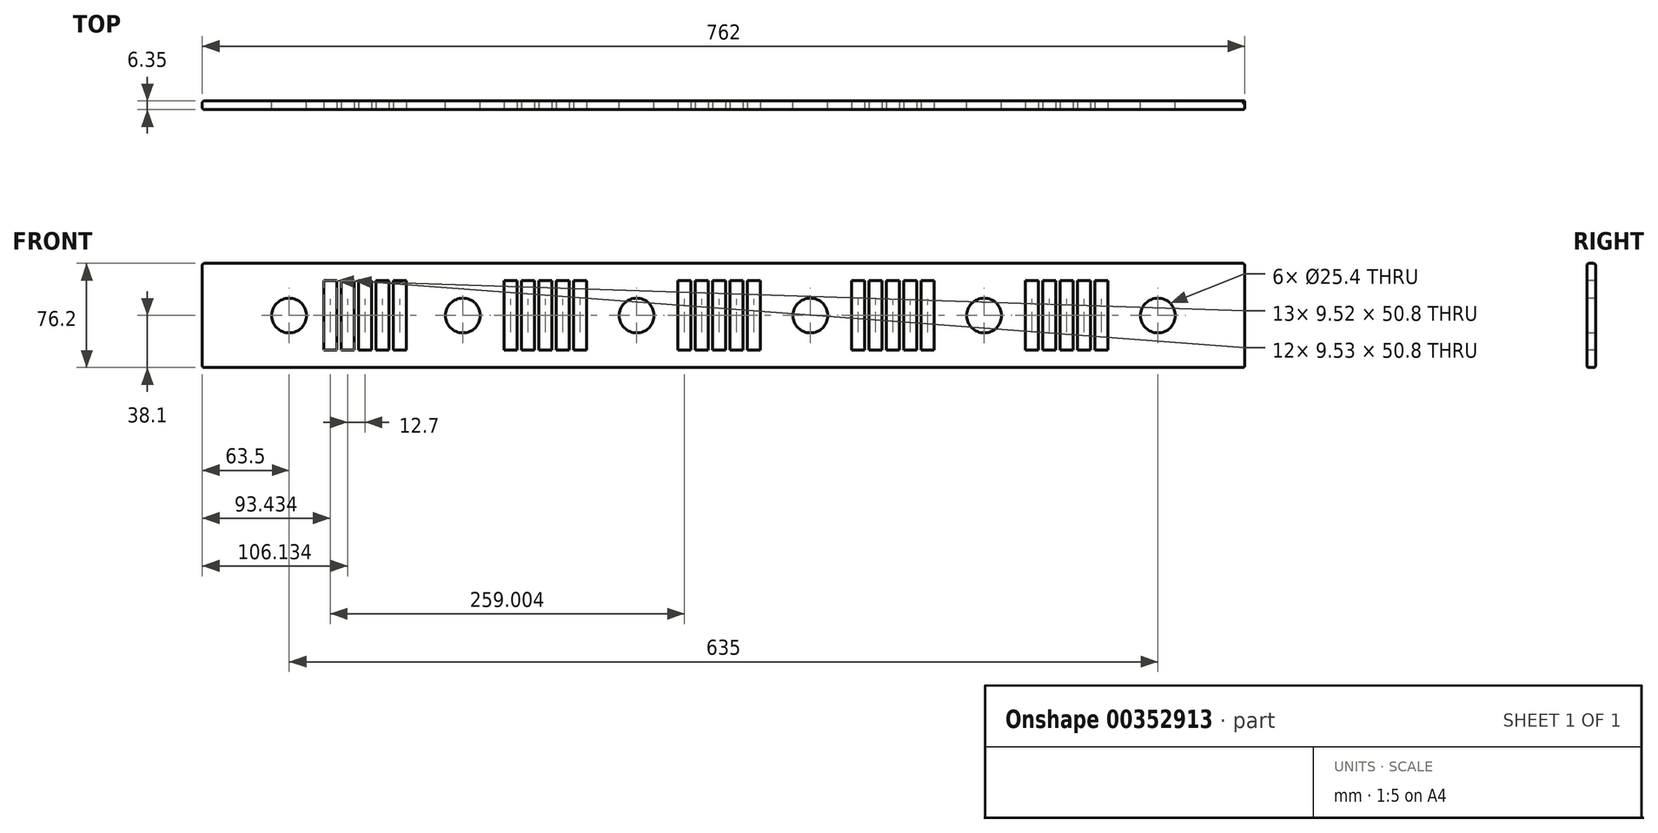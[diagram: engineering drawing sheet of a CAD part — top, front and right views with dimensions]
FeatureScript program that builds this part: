
annotation { "Feature Type Name" : "Feature", "Feature Type Description" : "" }
export const myFeature = defineFeature(function(context is Context, id is Id, definition is map)
    precondition{}
    {
        {
            var Q0;
            Q0=qCreatedBy(makeId("Front.planeOp"),FACE);
            var sketch = newSketch(context, id + "F0", { "sketchPlane" : qUnion([Q0])});
            skLineSegment(sketch, "E0.bottom", {"start": v(0, 0) * mm, "end": v(762, 0) * mm});
            skLineSegment(sketch, "E0.top", {"start": v(0, 76.2) * mm, "end": v(762, 76.2) * mm});
            skLineSegment(sketch, "E0.left", {"start": v(0, 0) * mm, "end": v(0, 76.2) * mm});
            skLineSegment(sketch, "E0.right", {"start": v(762, 0) * mm, "end": v(762, 76.2) * mm});
            skCircle(sketch, "E1", {"center": v(63.5, 38.1) * mm, "radius": 12.7 * mm});
            skPoint(sketch, "E1.centerSnap0", {"position": v(0, 38.1) * mm});
            skCircle(sketch, "E2", {"center": v(190.5, 38.1) * mm, "radius": 12.7 * mm});
            skCircle(sketch, "E3", {"center": v(317.5, 38.1) * mm, "radius": 12.7 * mm});
            skCircle(sketch, "E4", {"center": v(444.5, 38.1) * mm, "radius": 12.7 * mm});
            skCircle(sketch, "E5", {"center": v(571.5, 38.1) * mm, "radius": 12.7 * mm});
            skCircle(sketch, "E6", {"center": v(698.5, 38.1) * mm, "radius": 12.7 * mm});
            skSolve(sketch);
        }
        {
            var Q0;
            Q0=qSketchRegion(id+"F0",true);
            extrude(context, id + "F1", {"entities" : qUnion([Q0]), "depth" : 6.35 * mm});
        }
        {
            var Q0;
            Q0=makeQuery(id+"F1.opExtrude","CAP_FACE",FACE,{"disambiguationData":[OSD([sQuery(id+"F0.wireOp",EDGE,"E0.bottom"),sQuery(id+"F0.wireOp",EDGE,"E0.top"),sQuery(id+"F0.wireOp",EDGE,"E0.left"),sQuery(id+"F0.wireOp",EDGE,"E0.right"),sQuery(id+"F0.wireOp",EDGE,"E1"),sQuery(id+"F0.wireOp",EDGE,"E2"),sQuery(id+"F0.wireOp",EDGE,"E3"),sQuery(id+"F0.wireOp",EDGE,"E4"),sQuery(id+"F0.wireOp",EDGE,"E5"),sQuery(id+"F0.wireOp",EDGE,"E6")])],"isStart":false});
            var sketch = newSketch(context, id + "F2", { "sketchPlane" : qUnion([Q0])});
            skLineSegment(sketch, "E7.bottom", {"start": v(88.67, 12.7) * mm, "end": v(98.2, 12.7) * mm});
            skLineSegment(sketch, "E7.top", {"start": v(88.67, 63.5) * mm, "end": v(98.2, 63.5) * mm});
            skLineSegment(sketch, "E7.left", {"start": v(98.2, 12.7) * mm, "end": v(98.2, 63.5) * mm});
            skLineSegment(sketch, "E7.right", {"start": v(88.67, 12.7) * mm, "end": v(88.67, 63.5) * mm});
            skLineSegment(sketch, "E8.1.0.0", {"start": v(101.37, 12.7) * mm, "end": v(110.9, 12.7) * mm});
            skLineSegment(sketch, "E8.1.0.1", {"start": v(101.37, 63.5) * mm, "end": v(110.9, 63.5) * mm});
            skLineSegment(sketch, "E8.1.0.2", {"start": v(110.9, 12.7) * mm, "end": v(110.9, 63.5) * mm});
            skLineSegment(sketch, "E8.1.0.3", {"start": v(101.37, 12.7) * mm, "end": v(101.37, 63.5) * mm});
            skLineSegment(sketch, "E8.2.0.0", {"start": v(114.07, 12.7) * mm, "end": v(123.6, 12.7) * mm});
            skLineSegment(sketch, "E8.2.0.1", {"start": v(114.07, 63.5) * mm, "end": v(123.6, 63.5) * mm});
            skLineSegment(sketch, "E8.2.0.2", {"start": v(123.6, 12.7) * mm, "end": v(123.6, 63.5) * mm});
            skLineSegment(sketch, "E8.2.0.3", {"start": v(114.07, 12.7) * mm, "end": v(114.07, 63.5) * mm});
            skLineSegment(sketch, "E8.3.0.0", {"start": v(126.77, 12.7) * mm, "end": v(136.3, 12.7) * mm});
            skLineSegment(sketch, "E8.3.0.1", {"start": v(126.77, 63.5) * mm, "end": v(136.3, 63.5) * mm});
            skLineSegment(sketch, "E8.3.0.2", {"start": v(136.3, 12.7) * mm, "end": v(136.3, 63.5) * mm});
            skLineSegment(sketch, "E8.3.0.3", {"start": v(126.77, 12.7) * mm, "end": v(126.77, 63.5) * mm});
            skLineSegment(sketch, "E8.4.0.0", {"start": v(139.47, 12.7) * mm, "end": v(149, 12.7) * mm});
            skLineSegment(sketch, "E8.4.0.1", {"start": v(139.47, 63.5) * mm, "end": v(149, 63.5) * mm});
            skLineSegment(sketch, "E8.4.0.2", {"start": v(149, 12.7) * mm, "end": v(149, 63.5) * mm});
            skLineSegment(sketch, "E8.4.0.3", {"start": v(139.47, 12.7) * mm, "end": v(139.47, 63.5) * mm});
            skLineSegment(sketch, "E8.direction1", {"start": v(98.2, 12.7) * mm, "end": v(110.9, 12.7) * mm, "construction": true});
            skLineSegment(sketch, "E9.bottom", {"start": v(220.68, 12.7) * mm, "end": v(230.2, 12.7) * mm});
            skLineSegment(sketch, "E9.top", {"start": v(220.68, 63.5) * mm, "end": v(230.2, 63.5) * mm});
            skLineSegment(sketch, "E9.left", {"start": v(220.68, 12.7) * mm, "end": v(220.68, 63.5) * mm});
            skLineSegment(sketch, "E9.right", {"start": v(230.2, 12.7) * mm, "end": v(230.2, 63.5) * mm});
            skLineSegment(sketch, "E10.1.0.0", {"start": v(242.9, 12.7) * mm, "end": v(242.9, 63.5) * mm});
            skLineSegment(sketch, "E10.1.0.1", {"start": v(233.38, 12.7) * mm, "end": v(233.38, 63.5) * mm});
            skLineSegment(sketch, "E10.1.0.2", {"start": v(233.38, 63.5) * mm, "end": v(242.9, 63.5) * mm});
            skLineSegment(sketch, "E10.1.0.3", {"start": v(233.38, 12.7) * mm, "end": v(242.9, 12.7) * mm});
            skLineSegment(sketch, "E10.2.0.0", {"start": v(255.6, 12.7) * mm, "end": v(255.6, 63.5) * mm});
            skLineSegment(sketch, "E10.2.0.1", {"start": v(246.08, 12.7) * mm, "end": v(246.08, 63.5) * mm});
            skLineSegment(sketch, "E10.2.0.2", {"start": v(246.08, 63.5) * mm, "end": v(255.6, 63.5) * mm});
            skLineSegment(sketch, "E10.2.0.3", {"start": v(246.08, 12.7) * mm, "end": v(255.6, 12.7) * mm});
            skLineSegment(sketch, "E10.3.0.0", {"start": v(268.3, 12.7) * mm, "end": v(268.3, 63.5) * mm});
            skLineSegment(sketch, "E10.3.0.1", {"start": v(258.78, 12.7) * mm, "end": v(258.78, 63.5) * mm});
            skLineSegment(sketch, "E10.3.0.2", {"start": v(258.78, 63.5) * mm, "end": v(268.3, 63.5) * mm});
            skLineSegment(sketch, "E10.3.0.3", {"start": v(258.78, 12.7) * mm, "end": v(268.3, 12.7) * mm});
            skLineSegment(sketch, "E10.4.0.0", {"start": v(281, 12.7) * mm, "end": v(281, 63.5) * mm});
            skLineSegment(sketch, "E10.4.0.1", {"start": v(271.48, 12.7) * mm, "end": v(271.48, 63.5) * mm});
            skLineSegment(sketch, "E10.4.0.2", {"start": v(271.48, 63.5) * mm, "end": v(281, 63.5) * mm});
            skLineSegment(sketch, "E10.4.0.3", {"start": v(271.48, 12.7) * mm, "end": v(281, 12.7) * mm});
            skLineSegment(sketch, "E10.direction1", {"start": v(230.2, 12.7) * mm, "end": v(242.9, 12.7) * mm, "construction": true});
            skLineSegment(sketch, "E11.bottom", {"start": v(347.68, 12.7) * mm, "end": v(357.2, 12.7) * mm});
            skLineSegment(sketch, "E11.top", {"start": v(347.68, 63.5) * mm, "end": v(357.2, 63.5) * mm});
            skLineSegment(sketch, "E11.left", {"start": v(347.68, 12.7) * mm, "end": v(347.68, 63.5) * mm});
            skLineSegment(sketch, "E11.right", {"start": v(357.2, 12.7) * mm, "end": v(357.2, 63.5) * mm});
            skLineSegment(sketch, "E12.1.0.0", {"start": v(369.9, 12.7) * mm, "end": v(369.9, 63.5) * mm});
            skLineSegment(sketch, "E12.1.0.1", {"start": v(360.38, 12.7) * mm, "end": v(369.9, 12.7) * mm});
            skLineSegment(sketch, "E12.1.0.2", {"start": v(360.38, 12.7) * mm, "end": v(360.38, 63.5) * mm});
            skLineSegment(sketch, "E12.1.0.3", {"start": v(360.38, 63.5) * mm, "end": v(369.9, 63.5) * mm});
            skLineSegment(sketch, "E12.2.0.0", {"start": v(382.6, 12.7) * mm, "end": v(382.6, 63.5) * mm});
            skLineSegment(sketch, "E12.2.0.1", {"start": v(373.08, 12.7) * mm, "end": v(382.6, 12.7) * mm});
            skLineSegment(sketch, "E12.2.0.2", {"start": v(373.08, 12.7) * mm, "end": v(373.08, 63.5) * mm});
            skLineSegment(sketch, "E12.2.0.3", {"start": v(373.08, 63.5) * mm, "end": v(382.6, 63.5) * mm});
            skLineSegment(sketch, "E12.3.0.0", {"start": v(395.3, 12.7) * mm, "end": v(395.3, 63.5) * mm});
            skLineSegment(sketch, "E12.3.0.1", {"start": v(385.78, 12.7) * mm, "end": v(395.3, 12.7) * mm});
            skLineSegment(sketch, "E12.3.0.2", {"start": v(385.78, 12.7) * mm, "end": v(385.78, 63.5) * mm});
            skLineSegment(sketch, "E12.3.0.3", {"start": v(385.78, 63.5) * mm, "end": v(395.3, 63.5) * mm});
            skLineSegment(sketch, "E12.4.0.0", {"start": v(408, 12.7) * mm, "end": v(408, 63.5) * mm});
            skLineSegment(sketch, "E12.4.0.1", {"start": v(398.48, 12.7) * mm, "end": v(408, 12.7) * mm});
            skLineSegment(sketch, "E12.4.0.2", {"start": v(398.48, 12.7) * mm, "end": v(398.48, 63.5) * mm});
            skLineSegment(sketch, "E12.4.0.3", {"start": v(398.48, 63.5) * mm, "end": v(408, 63.5) * mm});
            skLineSegment(sketch, "E12.direction1", {"start": v(357.2, 12.7) * mm, "end": v(369.9, 12.7) * mm, "construction": true});
            skLineSegment(sketch, "E13.bottom", {"start": v(474.68, 12.7) * mm, "end": v(484.2, 12.7) * mm});
            skLineSegment(sketch, "E13.top", {"start": v(474.68, 63.5) * mm, "end": v(484.2, 63.5) * mm});
            skLineSegment(sketch, "E13.left", {"start": v(474.68, 12.7) * mm, "end": v(474.68, 63.5) * mm});
            skLineSegment(sketch, "E13.right", {"start": v(484.2, 12.7) * mm, "end": v(484.2, 63.5) * mm});
            skLineSegment(sketch, "E14.1.0.0", {"start": v(487.38, 12.7) * mm, "end": v(487.38, 63.5) * mm});
            skLineSegment(sketch, "E14.1.0.1", {"start": v(496.9, 12.7) * mm, "end": v(496.9, 63.5) * mm});
            skLineSegment(sketch, "E14.1.0.2", {"start": v(487.38, 12.7) * mm, "end": v(496.9, 12.7) * mm});
            skLineSegment(sketch, "E14.1.0.3", {"start": v(487.38, 63.5) * mm, "end": v(496.9, 63.5) * mm});
            skLineSegment(sketch, "E14.2.0.0", {"start": v(500.08, 12.7) * mm, "end": v(500.08, 63.5) * mm});
            skLineSegment(sketch, "E14.2.0.1", {"start": v(509.6, 12.7) * mm, "end": v(509.6, 63.5) * mm});
            skLineSegment(sketch, "E14.2.0.2", {"start": v(500.08, 12.7) * mm, "end": v(509.6, 12.7) * mm});
            skLineSegment(sketch, "E14.2.0.3", {"start": v(500.08, 63.5) * mm, "end": v(509.6, 63.5) * mm});
            skLineSegment(sketch, "E14.3.0.0", {"start": v(512.78, 12.7) * mm, "end": v(512.78, 63.5) * mm});
            skLineSegment(sketch, "E14.3.0.1", {"start": v(522.3, 12.7) * mm, "end": v(522.3, 63.5) * mm});
            skLineSegment(sketch, "E14.3.0.2", {"start": v(512.78, 12.7) * mm, "end": v(522.3, 12.7) * mm});
            skLineSegment(sketch, "E14.3.0.3", {"start": v(512.78, 63.5) * mm, "end": v(522.3, 63.5) * mm});
            skLineSegment(sketch, "E14.4.0.0", {"start": v(525.48, 12.7) * mm, "end": v(525.48, 63.5) * mm});
            skLineSegment(sketch, "E14.4.0.1", {"start": v(535, 12.7) * mm, "end": v(535, 63.5) * mm});
            skLineSegment(sketch, "E14.4.0.2", {"start": v(525.48, 12.7) * mm, "end": v(535, 12.7) * mm});
            skLineSegment(sketch, "E14.4.0.3", {"start": v(525.48, 63.5) * mm, "end": v(535, 63.5) * mm});
            skLineSegment(sketch, "E14.direction1", {"start": v(474.68, 12.7) * mm, "end": v(487.38, 12.7) * mm, "construction": true});
            skLineSegment(sketch, "E15.bottom", {"start": v(601.68, 12.7) * mm, "end": v(611.2, 12.7) * mm});
            skLineSegment(sketch, "E15.top", {"start": v(601.68, 63.5) * mm, "end": v(611.2, 63.5) * mm});
            skLineSegment(sketch, "E15.left", {"start": v(601.68, 12.7) * mm, "end": v(601.68, 63.5) * mm});
            skLineSegment(sketch, "E15.right", {"start": v(611.2, 12.7) * mm, "end": v(611.2, 63.5) * mm});
            skLineSegment(sketch, "E16.1.0.0", {"start": v(614.38, 12.7) * mm, "end": v(623.9, 12.7) * mm});
            skLineSegment(sketch, "E16.1.0.1", {"start": v(614.38, 12.7) * mm, "end": v(614.38, 63.5) * mm});
            skLineSegment(sketch, "E16.1.0.2", {"start": v(623.9, 12.7) * mm, "end": v(623.9, 63.5) * mm});
            skLineSegment(sketch, "E16.1.0.3", {"start": v(614.38, 63.5) * mm, "end": v(623.9, 63.5) * mm});
            skLineSegment(sketch, "E16.2.0.0", {"start": v(627.08, 12.7) * mm, "end": v(636.6, 12.7) * mm});
            skLineSegment(sketch, "E16.2.0.1", {"start": v(627.08, 12.7) * mm, "end": v(627.08, 63.5) * mm});
            skLineSegment(sketch, "E16.2.0.2", {"start": v(636.6, 12.7) * mm, "end": v(636.6, 63.5) * mm});
            skLineSegment(sketch, "E16.2.0.3", {"start": v(627.08, 63.5) * mm, "end": v(636.6, 63.5) * mm});
            skLineSegment(sketch, "E16.3.0.0", {"start": v(639.78, 12.7) * mm, "end": v(649.3, 12.7) * mm});
            skLineSegment(sketch, "E16.3.0.1", {"start": v(639.78, 12.7) * mm, "end": v(639.78, 63.5) * mm});
            skLineSegment(sketch, "E16.3.0.2", {"start": v(649.3, 12.7) * mm, "end": v(649.3, 63.5) * mm});
            skLineSegment(sketch, "E16.3.0.3", {"start": v(639.78, 63.5) * mm, "end": v(649.3, 63.5) * mm});
            skLineSegment(sketch, "E16.4.0.0", {"start": v(652.48, 12.7) * mm, "end": v(662, 12.7) * mm});
            skLineSegment(sketch, "E16.4.0.1", {"start": v(652.48, 12.7) * mm, "end": v(652.48, 63.5) * mm});
            skLineSegment(sketch, "E16.4.0.2", {"start": v(662, 12.7) * mm, "end": v(662, 63.5) * mm});
            skLineSegment(sketch, "E16.4.0.3", {"start": v(652.48, 63.5) * mm, "end": v(662, 63.5) * mm});
            skLineSegment(sketch, "E16.direction1", {"start": v(601.68, 12.7) * mm, "end": v(614.38, 12.7) * mm, "construction": true});
            skSolve(sketch);
        }
        {
            var Q0;
            Q0=qSketchRegion(id+"F2",true);
            extrude(context, id + "F3", {"entities" : qUnion([Q0]), "operationType" : NewBodyOperationType.REMOVE, "endBound" : BoundingType.THROUGH_ALL, "oppositeDirection" : true, "depth" : 25.4 * mm});
        }
        {
            var Q0;
            Q0=makeQuery(id+"F1.opExtrude","CAP_EDGE",EDGE,{"disambiguationData":[OSD([sQuery(id+"F0.wireOp",EDGE,"E0.top")])],"isStart":false});
            var Q1;
            Q1=makeQuery(id+"F1.opExtrude","CAP_EDGE",EDGE,{"disambiguationData":[OSD([sQuery(id+"F0.wireOp",EDGE,"E0.top")])],"isStart":true});
            var Q2;
            Q2=makeQuery(id+"F1.opExtrude","CAP_EDGE",EDGE,{"disambiguationData":[OSD([sQuery(id+"F0.wireOp",EDGE,"E0.left")])],"isStart":false});
            var Q3;
            Q3=makeQuery(id+"F1.opExtrude","CAP_EDGE",EDGE,{"disambiguationData":[OSD([sQuery(id+"F0.wireOp",EDGE,"E0.left")])],"isStart":true});
            var Q4;
            Q4=makeQuery(id+"F1.opExtrude","SWEPT_FACE",FACE,{"disambiguationData":[OSD([sQuery(id+"F0.wireOp",EDGE,"E0.top")])]});
            var Q5;
            Q5=makeQuery(id+"F1.opExtrude","SWEPT_EDGE",EDGE,{"disambiguationData":[OSD([sQuery(id+"F0.wireOp",EDGE,"E0.bottom"),sQuery(id+"F0.wireOp",EDGE,"E0.left")])]});
            var Q6;
            Q6=makeQuery(id+"F1.opExtrude","CAP_EDGE",EDGE,{"disambiguationData":[OSD([sQuery(id+"F0.wireOp",EDGE,"E0.bottom")])],"isStart":false});
            var Q7;
            Q7=makeQuery(id+"F1.opExtrude","CAP_EDGE",EDGE,{"disambiguationData":[OSD([sQuery(id+"F0.wireOp",EDGE,"E0.bottom")])],"isStart":true});
            var Q8;
            Q8=makeQuery(id+"F1.opExtrude","SWEPT_EDGE",EDGE,{"disambiguationData":[OSD([sQuery(id+"F0.wireOp",EDGE,"E0.bottom"),sQuery(id+"F0.wireOp",EDGE,"E0.right")])]});
            var Q9;
            Q9=makeQuery(id+"F1.opExtrude","CAP_EDGE",EDGE,{"disambiguationData":[OSD([sQuery(id+"F0.wireOp",EDGE,"E0.right")])],"isStart":false});
            var Q10;
            Q10=makeQuery(id+"F1.opExtrude","SWEPT_EDGE",EDGE,{"disambiguationData":[OSD([sQuery(id+"F0.wireOp",EDGE,"E0.top"),sQuery(id+"F0.wireOp",EDGE,"E0.right")])]});
            fillet(context, id + "F4", {"entities" : qUnion([Q0, Q1, Q2, Q3, Q4, Q5, Q6, Q7, Q8, Q9, Q10]), "radius" : 1.6 * mm, "tangentPropagation" : true, "allowEdgeOverflow" : false});
        }
    });
